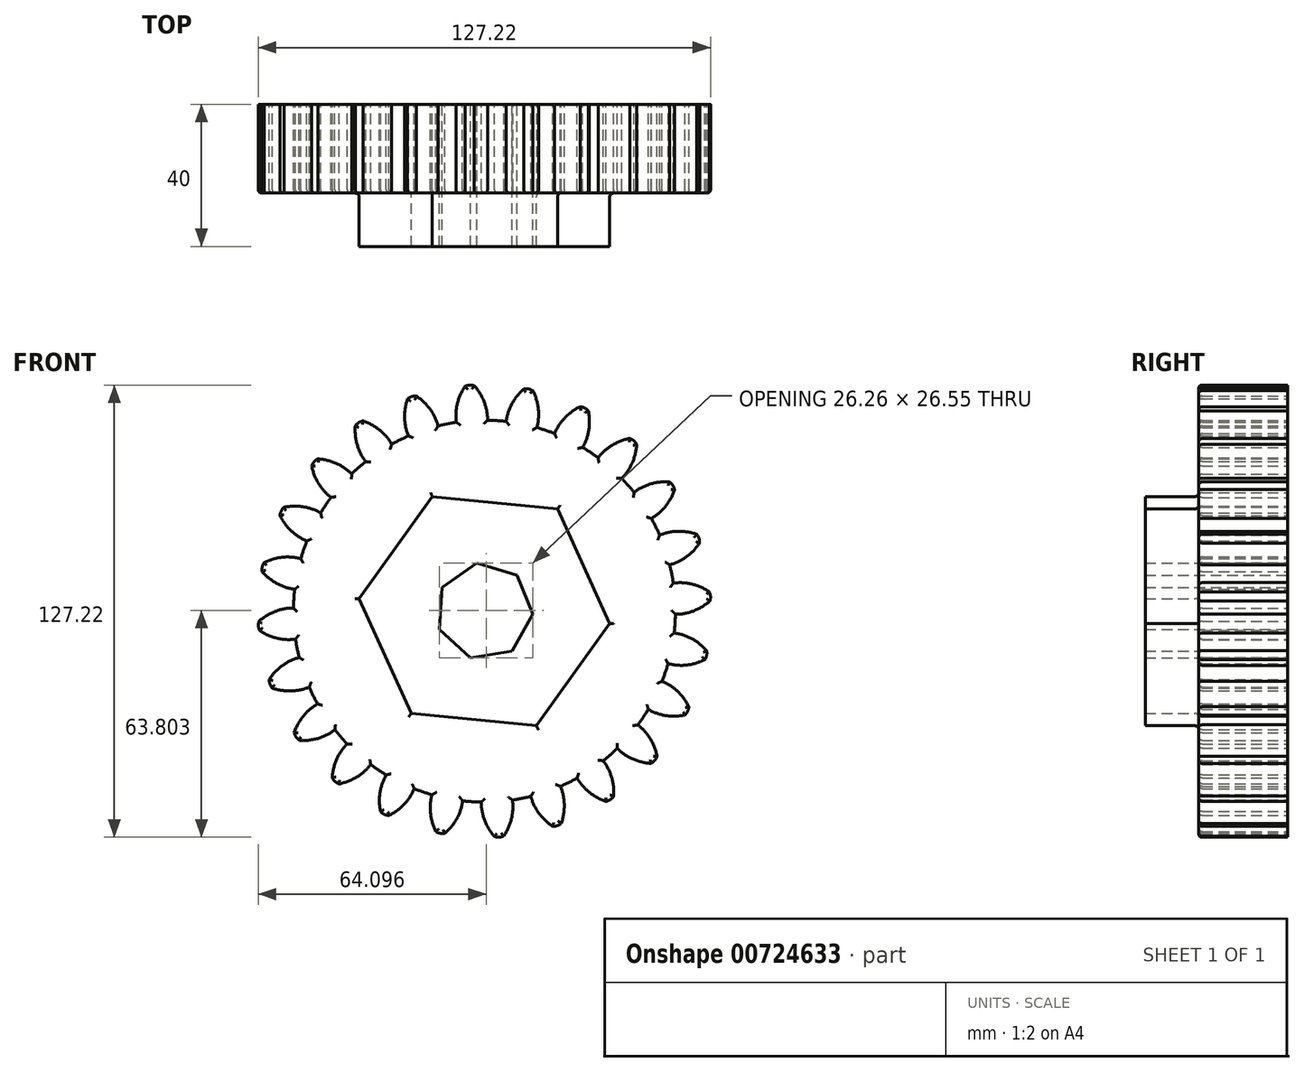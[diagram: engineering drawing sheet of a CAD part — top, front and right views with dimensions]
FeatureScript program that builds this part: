
annotation { "Feature Type Name" : "Feature", "Feature Type Description" : "" }
export const myFeature = defineFeature(function(context is Context, id is Id, definition is map)
    precondition{}
    {
        {
            var Q0;
            Q0=qCreatedBy(makeId("Front.planeOp"),FACE);
            var sketch = newSketch(context, id + "F0", { "sketchPlane" : qUnion([Q0])});
            skCircle(sketch, "E0", {"center": v(0, 0) * mm, "radius": 53.72 * mm});
            skCircle(sketch, "E1", {"center": v(0, 0) * mm, "radius": 58.67 * mm, "construction": true});
            skCircle(sketch, "E2", {"center": v(0, 0) * mm, "radius": 63.5 * mm, "construction": true});
            skLineSegment(sketch, "E3", {"start": v(0, 0) * mm, "end": v(0, 100.95) * mm, "construction": true});
            skLineSegment(sketch, "E4", {"start": v(0, 0) * mm, "end": v(-5.95, 90.82) * mm, "construction": true});
            skLineSegment(sketch, "E5", {"start": v(0, 58.67) * mm, "end": v(-49.43, 58.67) * mm, "construction": true});
            skLineSegment(sketch, "E6", {"start": v(0, 58.67) * mm, "end": v(-58.4, 37.42) * mm, "construction": true});
            skCircle(sketch, "E7", {"center": v(0, 0) * mm, "radius": 55.14 * mm, "construction": true});
            skCircle(sketch, "E8", {"center": v(0, 58.67) * mm, "radius": 14.6 * mm, "construction": true});
            skCircle(sketch, "E9", {"center": v(-13.72, 53.68) * mm, "radius": 14.6 * mm, "construction": true});
            skArc(sketch, "E10", {"start": v(0, 58.67) * mm, "mid": v(-1.2, 61.19) * mm, "end": v(-2.86, 63.44) * mm});
            skArc(sketch, "E11", {"start": v(0.88, 53.71) * mm, "mid": v(0.67, 56.23) * mm, "end": v(0, 58.67) * mm});
            skArc(sketch, "E12.MirrorCS", {"start": v(-7.66, 58.17) * mm, "mid": v(-6.79, 60.82) * mm, "end": v(-5.45, 63.27) * mm});
            skArc(sketch, "E13.MirrorCS", {"start": v(-7.88, 53.14) * mm, "mid": v(-8, 55.67) * mm, "end": v(-7.66, 58.17) * mm});
            skArc(sketch, "E14", {"start": v(-2.86, 63.44) * mm, "mid": v(-4.17, 63.6) * mm, "end": v(-5.45, 63.27) * mm});
            skCircle(sketch, "E15.cCircle", {"center": v(0, 0) * mm, "radius": 30.67 * mm, "construction": true});
            skLineSegment(sketch, "E15.0", {"start": v(-20.6, -28.8) * mm, "end": v(-35.25, 3.45) * mm});
            skLineSegment(sketch, "E15.1", {"start": v(-35.25, 3.45) * mm, "end": v(-14.64, 32.25) * mm});
            skLineSegment(sketch, "E15.2", {"start": v(-14.64, 32.25) * mm, "end": v(20.6, 28.8) * mm});
            skLineSegment(sketch, "E15.3", {"start": v(20.6, 28.8) * mm, "end": v(35.25, -3.45) * mm});
            skLineSegment(sketch, "E15.4", {"start": v(35.25, -3.45) * mm, "end": v(14.64, -32.25) * mm});
            skLineSegment(sketch, "E15.5", {"start": v(14.64, -32.25) * mm, "end": v(-20.6, -28.8) * mm});
            skPoint(sketch, "E15.0.midPoint", {"position": v(-27.93, -12.68) * mm});
            skCircle(sketch, "E16.cCircle", {"center": v(0, 0) * mm, "radius": 12.3 * mm, "construction": true});
            skLineSegment(sketch, "E16.0", {"start": v(-3.88, -13.08) * mm, "end": v(-12.64, -5.13) * mm});
            skLineSegment(sketch, "E16.1", {"start": v(-12.64, -5.13) * mm, "end": v(-11.9, 6.69) * mm});
            skLineSegment(sketch, "E16.2", {"start": v(-11.9, 6.69) * mm, "end": v(-2.19, 13.47) * mm});
            skLineSegment(sketch, "E16.3", {"start": v(-2.19, 13.47) * mm, "end": v(9.17, 10.1) * mm});
            skLineSegment(sketch, "E16.4", {"start": v(9.17, 10.1) * mm, "end": v(13.62, -0.87) * mm});
            skLineSegment(sketch, "E16.5", {"start": v(13.62, -0.87) * mm, "end": v(7.81, -11.19) * mm});
            skLineSegment(sketch, "E16.6", {"start": v(7.81, -11.19) * mm, "end": v(-3.88, -13.08) * mm});
            skPoint(sketch, "E16.0.midPoint", {"position": v(-8.26, -9.1) * mm});
            skSolve(sketch);
        }
        {
            var Q0;
            {var subQ0=sQuery(id+"F0.wireOp",EDGE,"E0");var subQ1=makeQuery(id+"F0.imprint","INTERSECT",VERTEX,{"derivedFrom":[subQ0,sQuery(id+"F0.wireOp",EDGE,"E11")]});Q0=makeQuery(id+"F0.imprint","IMPRINT",FACE,{"disambiguationData":[TD([[makeQuery(id+"F0.imprint","IMPRINT",EDGE,{"disambiguationData":[TD([[subQ1,-1.0]])],"derivedFrom":subQ0}),1.0]])]});}
            var Q1;
            Q1=makeQuery(id+"F0.imprint","IMPRINT",FACE,{"disambiguationData":[TD([[makeQuery(id+"F0.imprint","IMPRINT",EDGE,{"derivedFrom":sQuery(id+"F0.wireOp",EDGE,"E10")}),1.0]])]});
            extrude(context, id + "F1", {"entities" : qUnion([Q0, Q1]), "depth" : 25 * mm, "offsetDistance" : 25 * mm});
        }
        {
            var Q0;
            Q0=makeQuery(id+"F1.opExtrude","SWEPT_BODY",BODY,{"disambiguationData":[OSD([sQuery(id+"F0.wireOp",EDGE,"E0"),sQuery(id+"F0.wireOp",EDGE,"E10"),sQuery(id+"F0.wireOp",EDGE,"E11"),sQuery(id+"F0.wireOp",EDGE,"E12.MirrorCS"),sQuery(id+"F0.wireOp",EDGE,"E13.MirrorCS"),sQuery(id+"F0.wireOp",EDGE,"E14")])]});
            var Q1;
            Q1=makeQuery(id+"F1.opExtrude","SWEPT_FACE",FACE,{"disambiguationData":[OSD([sQuery(id+"F0.wireOp",EDGE,"E0")])]});
            circularPattern(context, id + "F2", {"entities" : qUnion([Q0]), "axis" : qUnion([Q1]), "angle" : 360 * degree, "instanceCount" : 24, "equalSpace" : true});
        }
        {
            var Q0;
            Q0=makeQuery(id+"F0.imprint","IMPRINT",FACE,{"disambiguationData":[TD([[makeQuery(id+"F0.imprint","IMPRINT",EDGE,{"derivedFrom":sQuery(id+"F0.wireOp",EDGE,"E15.0")}),-1.0]])]});
            extrude(context, id + "F3", {"entities" : qUnion([Q0]), "operationType" : NewBodyOperationType.ADD, "depth" : 40 * mm, "offsetDistance" : 25 * mm});
        }
        {
            var Q0;
            {var subQ0=makeQuery(id+"F1.opExtrude","CAP_FACE",FACE,{"disambiguationData":[OSD([sQuery(id+"F0.wireOp",EDGE,"E0"),sQuery(id+"F0.wireOp",EDGE,"E10"),sQuery(id+"F0.wireOp",EDGE,"E11"),sQuery(id+"F0.wireOp",EDGE,"E12.MirrorCS"),sQuery(id+"F0.wireOp",EDGE,"E13.MirrorCS"),sQuery(id+"F0.wireOp",EDGE,"E14"),sQuery(id+"F0.wireOp",EDGE,"E15.0"),sQuery(id+"F0.wireOp",EDGE,"E15.1"),sQuery(id+"F0.wireOp",EDGE,"E15.2"),sQuery(id+"F0.wireOp",EDGE,"E15.3"),sQuery(id+"F0.wireOp",EDGE,"E15.4"),sQuery(id+"F0.wireOp",EDGE,"E15.5")])],"isStart":false});Q0=makeQuery(id+"F3.boolean.opBoolean","MERGE",FACE,{"derivedFrom":[subQ0,makeQuery(id+"F2.opPattern","COPY",FACE,{"derivedFrom":subQ0,"instanceName":"1"}),makeQuery(id+"F2.opPattern","COPY",FACE,{"derivedFrom":subQ0,"instanceName":"2"}),makeQuery(id+"F2.opPattern","COPY",FACE,{"derivedFrom":subQ0,"instanceName":"3"}),makeQuery(id+"F2.opPattern","COPY",FACE,{"derivedFrom":subQ0,"instanceName":"4"}),makeQuery(id+"F2.opPattern","COPY",FACE,{"derivedFrom":subQ0,"instanceName":"5"}),makeQuery(id+"F2.opPattern","COPY",FACE,{"derivedFrom":subQ0,"instanceName":"6"}),makeQuery(id+"F2.opPattern","COPY",FACE,{"derivedFrom":subQ0,"instanceName":"7"}),makeQuery(id+"F2.opPattern","COPY",FACE,{"derivedFrom":subQ0,"instanceName":"8"}),makeQuery(id+"F2.opPattern","COPY",FACE,{"derivedFrom":subQ0,"instanceName":"9"}),makeQuery(id+"F2.opPattern","COPY",FACE,{"derivedFrom":subQ0,"instanceName":"10"}),makeQuery(id+"F2.opPattern","COPY",FACE,{"derivedFrom":subQ0,"instanceName":"11"}),makeQuery(id+"F2.opPattern","COPY",FACE,{"derivedFrom":subQ0,"instanceName":"12"}),makeQuery(id+"F2.opPattern","COPY",FACE,{"derivedFrom":subQ0,"instanceName":"13"}),makeQuery(id+"F2.opPattern","COPY",FACE,{"derivedFrom":subQ0,"instanceName":"14"}),makeQuery(id+"F2.opPattern","COPY",FACE,{"derivedFrom":subQ0,"instanceName":"15"}),makeQuery(id+"F2.opPattern","COPY",FACE,{"derivedFrom":subQ0,"instanceName":"16"}),makeQuery(id+"F2.opPattern","COPY",FACE,{"derivedFrom":subQ0,"instanceName":"17"}),makeQuery(id+"F2.opPattern","COPY",FACE,{"derivedFrom":subQ0,"instanceName":"18"}),makeQuery(id+"F2.opPattern","COPY",FACE,{"derivedFrom":subQ0,"instanceName":"19"}),makeQuery(id+"F2.opPattern","COPY",FACE,{"derivedFrom":subQ0,"instanceName":"20"}),makeQuery(id+"F2.opPattern","COPY",FACE,{"derivedFrom":subQ0,"instanceName":"21"}),makeQuery(id+"F2.opPattern","COPY",FACE,{"derivedFrom":subQ0,"instanceName":"22"}),makeQuery(id+"F2.opPattern","COPY",FACE,{"derivedFrom":subQ0,"instanceName":"23"})]});}
            fillet(context, id + "F4", {"entities" : qUnion([Q0]), "radius" : 1 * mm, "tangentPropagation" : true, "allowEdgeOverflow" : false});
        }
    });
